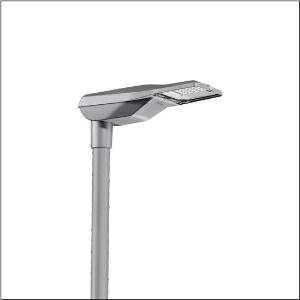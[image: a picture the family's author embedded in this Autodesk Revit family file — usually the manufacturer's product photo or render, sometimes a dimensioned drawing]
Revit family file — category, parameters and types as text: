
# Revit family: streetlight_sl_21_iq_micro___p0_8ab_5xe1r31g08db_e4e9
name_source: partatom
category: Lighting Fixtures
units: mm (PartAtom-declared; Revit-internal decimal feet)

## family parameters
Cut with Voids When Loaded = No
Host = Face
Light Source = No
Part Type = Normal
Room Calculation Point = No
Round Connector Dimension = Use Diameter
Shared = No

## types (1)
- --- (1 x LED, 4220 lm, 36.4 W, 3000K)
    Apparent Load = 36 VA
    CIE Flux Codes = 36 71 98 100 100
    Color Rendering = 70
    Color Temperature = 3000K
    Default Elevation = 1800 mm
    Description = Streetlight SL 21 iQ micro, mast luminaire, primary light control with lens, of PMMA, primary optical cover: cover, of toughened safety glass, transparent, light distribution: P0.8aB, light emission: direct distribution, primary light characteristic: asymmetric, installation type: post-top, side-entry, LED, High Power LED, rated luminous flux: 4.220lm, luminous efficacy: 116lm/W, light colour: 730, colour temperature: 3000K, control gear: iQ Street-Remote, control: pre-setting: linear dimming characteristic, Street-Remote, Auto-Match, Temp-Guard, Lumen-Switch, Night-Set, Smart-Wire, Light-Fading, Desk-Remote (wireless, voltage-free reading and setting of iQ features in the workshop via application-optimized NFC function/RFID function), optimised constant luminous flux control (CLO 2.0), mains connection: 220..240V, AC, 50/60Hz, start of lifetime: 36W, end of service life: 38W, reduction: 16W, luminaire housing, of diecast aluminium, powder-coated, SITECO metallic grey (DB 702S), corrosivity category C5 high according to DIN EN ISO 12944, please order mast flange separately, inclination adjustable: 0°, 5°, 10°, 15°, sealing non-destructively replaceable, multi-level sealing system, length: 528mm, width: 235mm, height: 110mm, mast flange for spigot size: 42mm (side-entry): 5XC10008XM4, 60/48mm (side-entry/post-top): 5XC10108XM2, 76/60mm (side-entry/post-top): 5XC10108XM1, protection rating (complete): IP66, insulation class (complete): insulation class II (safety insulation), certification: CE, ENEC, ENEC+, VDE, impact resistance: IK10, permissible operating ambient temperature for outdoor applications: -40..+50°C, standard-compliant lighting for roads and squares, packaging unit: 1 piece

Light Distribution: P0.8aB
    Height = 110 mm
    Lamp = 1 x LED
    Lamp Light Flux = 4220 lm
    Lamp Power = 36.4 W
    Lamp count = 1
    Length = 528 mm
    Luminous efficacy = 116 lm/W
    Manufacturer = Siteco
    ModVariant = No
    Model = 5XE1R31G08DB
    Mounting Place = Pole
    Mounting Type = Pole top
    Number of Poles = 1
    OnlyDefault = Yes
    Power Factor = 1
    Product Name = Streetlight SL 21 iQ micro | P0.8aB
    Product group = mast luminaire | pylon top
    ProductGroupID = 6100
    Protection Class = Protection class II
    Protection Degree = IP 66
    RLX_Detail_Level = 1
    RLX_Emergency_Light_Flux = 0 lm
    RLX_Emergency_Type = 0
    RLX_Emergency_Type_DB = No
    RlxData = <blob elided: 98597 chars, md5=64e0b52b>
    Socket = socket
    Standby Power = 0 W
    System Light Flux = 4220 lm
    System Power = 36 W
    Type Comments = factory setting: luminous flux: 100 % | dim-lin: 254 | 715 mA
    Type Image = l_1006881.jpg
    URL = http://relux.com
    VarID = @adj_084087
    Voltage = 0 V
    Weight = 0.00 kg
    Width = 235 mm

## geometry (parser evidence)
native form markers: Blend x4, Sweep x12
no freeform markers — native parametric forms only
